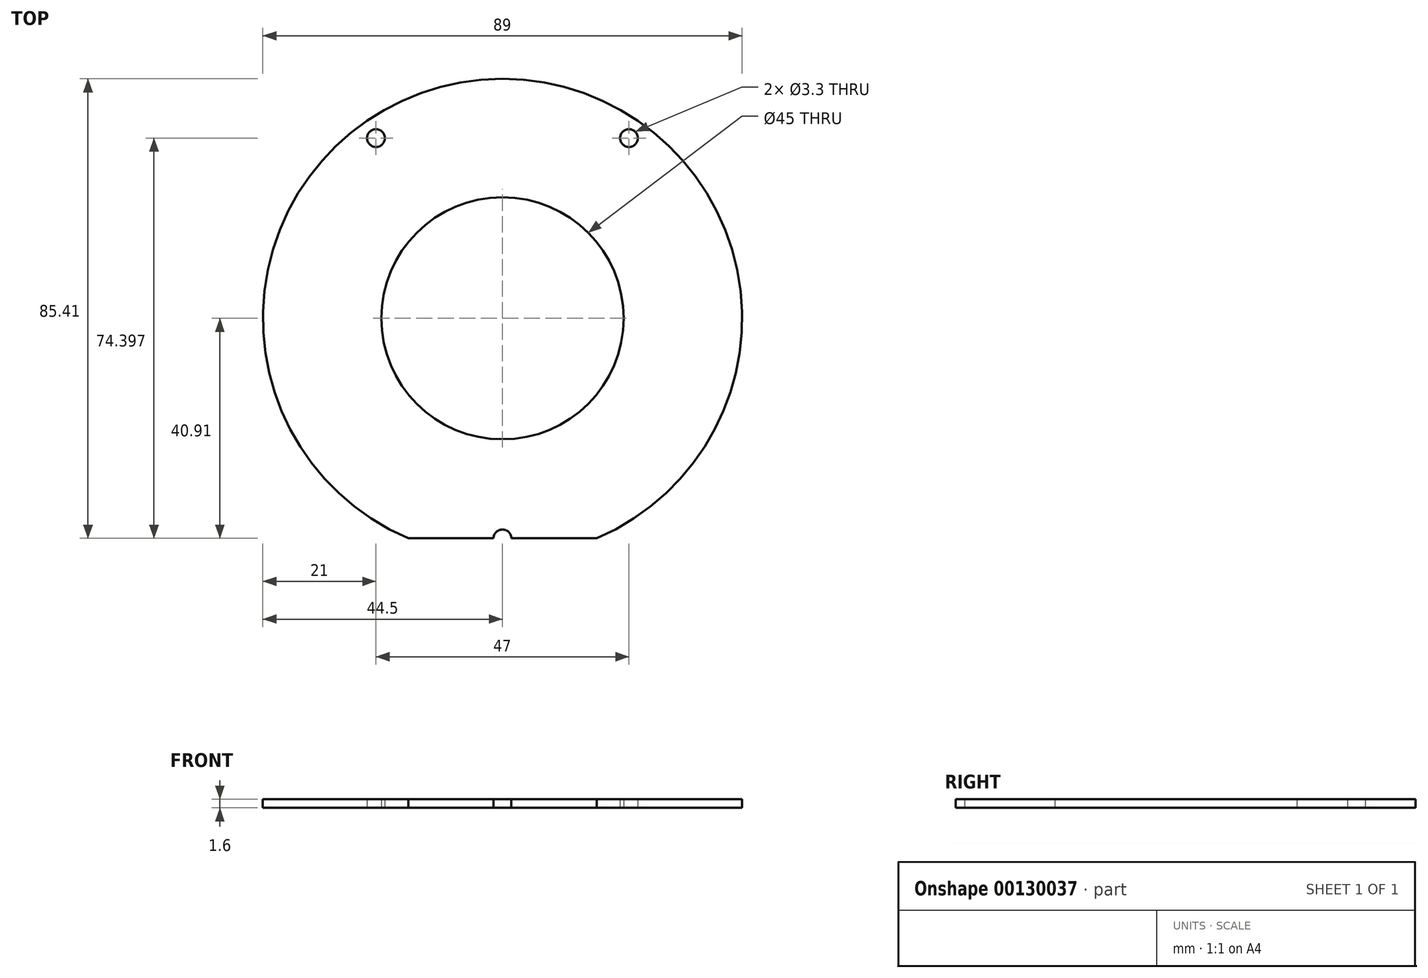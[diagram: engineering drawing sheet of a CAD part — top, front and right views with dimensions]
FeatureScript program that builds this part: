
annotation { "Feature Type Name" : "Feature", "Feature Type Description" : "" }
export const myFeature = defineFeature(function(context is Context, id is Id, definition is map)
    precondition{}
    {
        {
            var Q0;
            Q0=qCreatedBy(makeId("Top.planeOp"),FACE);
            var sketch = newSketch(context, id + "F0", { "sketchPlane" : qUnion([Q0])});
            skCircle(sketch, "E0", {"center": v(0, 0) * mm, "radius": 44.5 * mm});
            skCircle(sketch, "E1", {"center": v(0, 0) * mm, "radius": 22.5 * mm});
            skLineSegment(sketch, "E2.bottom", {"start": v(23.5, 33.49) * mm, "end": v(-23.5, 33.49) * mm});
            skLineSegment(sketch, "E2.top", {"start": v(23.5, -40.91) * mm, "end": v(-23.5, -40.91) * mm});
            skLineSegment(sketch, "E2.left", {"start": v(23.5, 33.49) * mm, "end": v(23.5, -40.91) * mm});
            skLineSegment(sketch, "E2.right", {"start": v(-23.5, 33.49) * mm, "end": v(-23.5, -40.91) * mm});
            skPoint(sketch, "E2.middle", {"position": v(0, -3.71) * mm});
            skCircle(sketch, "E3", {"center": v(0, -40.91) * mm, "radius": 1.65 * mm});
            skCircle(sketch, "E4", {"center": v(-23.5, 33.49) * mm, "radius": 1.65 * mm});
            skCircle(sketch, "E5", {"center": v(23.5, 33.49) * mm, "radius": 1.65 * mm});
            skSolve(sketch);
        }
        {
            var Q0;
            {var subQ1=sQuery(id+"F0.wireOp",EDGE,"E0");var subQ9=sQuery(id+"F0.wireOp",EDGE,"E2.right");var subQ10=makeQuery(id+"F0.imprint","INTERSECT",VERTEX,{"derivedFrom":[subQ1,subQ9]});Q0=makeQuery(id+"F0.imprint","IMPRINT",FACE,{"disambiguationData":[TD([[makeQuery(id+"F0.imprint","IMPRINT",EDGE,{"disambiguationData":[TD([[subQ10,1.0]])],"derivedFrom":subQ1}),1.0]])]});}
            var Q1;
            Q1=makeQuery(id+"F0.imprint","IMPRINT",FACE,{"disambiguationData":[TD([[makeQuery(id+"F0.imprint","IMPRINT",EDGE,{"derivedFrom":sQuery(id+"F0.wireOp",EDGE,"E1")}),-1.0]])]});
            var Q2;
            {var subQ0=sQuery(id+"F0.wireOp",EDGE,"E2.top");var subQ1=sQuery(id+"F0.wireOp",EDGE,"E0");var subQ2=makeQuery(id+"F0.imprint","INTERSECT",VERTEX,{"disambiguationData":[OD(0.0)],"derivedFrom":[subQ1,subQ0]});Q2=makeQuery(id+"F0.imprint","IMPRINT",FACE,{"disambiguationData":[TD([[makeQuery(id+"F0.imprint","IMPRINT",EDGE,{"disambiguationData":[TD([[subQ2,-1.0]])],"derivedFrom":subQ1}),1.0]])]});}
            extrude(context, id + "F1", {"entities" : qUnion([Q0, Q1, Q2]), "depth" : 1.6 * mm});
        }
    });
